# Revit family: Astro _XXX _ Sabina Square
name_source: partatom
category: Lighting Fixtures
revit_build: Autodesk Revit 2018 (Build: 20170223_1515(x64)
units: mm (PartAtom-declared; Revit-internal decimal feet)

## family parameters
Always vertical = Yes
Cut with Voids When Loaded = No
Host = Ceiling
Light Source = No
OmniClass Number = 23.80.70.11
OmniClass Title = Luminaries for Internal Lighting
Part Type = Normal
Room Calculation Point = No
Round Connector Dimension = Use Diameter
Shared = No

## types (1)
- Astro _ Sabina Square
    Dimmable = Lamp Dependant
    Dimming Method = Lamp Dependant
    Efficacy (lm/w) = Lamp Dependant
    Electrical Class = II
    Lamp = E27 LED
    Light Source Fixed = 12 Watt MAX
    Location / IP Rating = IP44
    Main Finish = Glass / Chrome
    Main Material = White Glass
    Manufacturer URL - Europe and Rest of World = www.astrolighting.com
    Manufacturer URL - North America = us.astrolighting.com
    Power (Watts) = 12 W
    Product CCT = Lamp Dependant
    Product CRI = Lamp Dependant
    Product Dimensions (MM) = 175 x 175 x 175
    Product Location = Zone 2, 3
    Product Name = Sabina Square
    Product SKU = 1292002
    Product URL = https://www.astrolighting.com
    Product Weight (KG) = 2 mm  [stored 0.00656168 ft]

note: [stored X ft] marks values corroborated as IEEE doubles in the binary element streams (Revit-internal decimal feet)

## geometry (parser evidence)
native form markers: Sweep x2
no freeform markers — native parametric forms only
